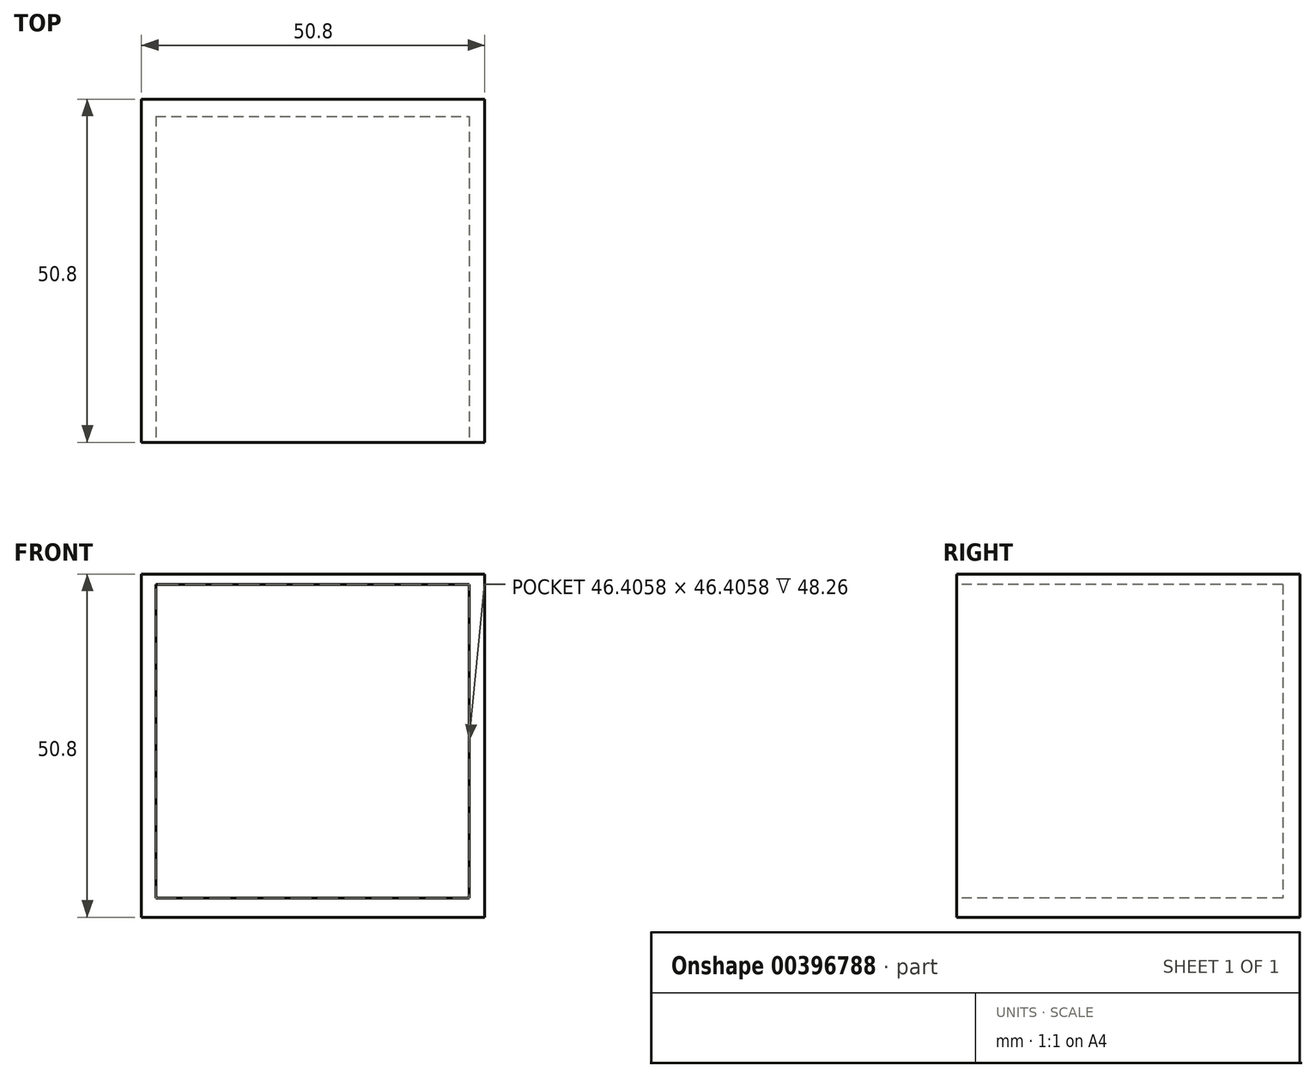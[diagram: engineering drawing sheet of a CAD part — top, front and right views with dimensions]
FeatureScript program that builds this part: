
annotation { "Feature Type Name" : "Feature", "Feature Type Description" : "" }
export const myFeature = defineFeature(function(context is Context, id is Id, definition is map)
    precondition{}
    {
        {
            var Q0;
            Q0=qCreatedBy(makeId("Front.planeOp"),FACE);
            var sketch = newSketch(context, id + "F0", { "sketchPlane" : qUnion([Q0])});
            skLineSegment(sketch, "E0.bottom", {"start": v(0, 0) * mm, "end": v(-50.8, 0) * mm});
            skLineSegment(sketch, "E0.top", {"start": v(0, 50.8) * mm, "end": v(-50.8, 50.8) * mm});
            skLineSegment(sketch, "E0.left", {"start": v(0, 0) * mm, "end": v(0, 50.8) * mm});
            skLineSegment(sketch, "E0.right", {"start": v(-50.8, 0) * mm, "end": v(-50.8, 50.8) * mm});
            skSolve(sketch);
        }
        {
            var Q0;
            Q0 = qSketchRegion(id + "F0", true);
            extrude(context, id + "F1", {"entities" : qUnion([Q0]), "depth" : 50.8 * mm});
        }
        {
            var Q0;
            Q0=makeQuery(id+"F1.opExtrude","CAP_FACE",FACE,{"disambiguationData":[OSD([sQuery(id+"F0.wireOp",EDGE,"E0.bottom"),sQuery(id+"F0.wireOp",EDGE,"E0.top"),sQuery(id+"F0.wireOp",EDGE,"E0.left"),sQuery(id+"F0.wireOp",EDGE,"E0.right")])],"isStart":false});
            var sketch = newSketch(context, id + "F2", { "sketchPlane" : qUnion([Q0])});
            skSolve(sketch);
        }
        {
            var Q0;
            Q0=makeQuery(id+"F2.imprint","IMPRINT",FACE,{"disambiguationData":[TD([[makeQuery(id+"F2.imprint","IMPRINT",EDGE,{"derivedFrom":makeQuery(id+"F1.opExtrude","CAP_EDGE",EDGE,{"disambiguationData":[OSD([sQuery(id+"F0.wireOp",EDGE,"E0.bottom")])],"isStart":false})}),-1.0]])]});
            var sketch = newSketch(context, id + "F3", { "sketchPlane" : qUnion([Q0])});
            skLineSegment(sketch, "E1.bottom", {"start": v(-48.7, 49.27) * mm, "end": v(-2.29, 49.27) * mm});
            skLineSegment(sketch, "E1.top", {"start": v(-48.7, 2.86) * mm, "end": v(-2.29, 2.86) * mm});
            skLineSegment(sketch, "E1.left", {"start": v(-48.7, 49.27) * mm, "end": v(-48.7, 2.86) * mm});
            skLineSegment(sketch, "E1.right", {"start": v(-2.29, 49.27) * mm, "end": v(-2.29, 2.86) * mm});
            skSolve(sketch);
        }
        {
            var Q0;
            Q0 = qSketchRegion(id + "F3", true);
            extrude(context, id + "F4", {"entities" : qUnion([Q0]), "operationType" : NewBodyOperationType.REMOVE, "oppositeDirection" : true, "depth" : 48.26 * mm});
        }
    });
